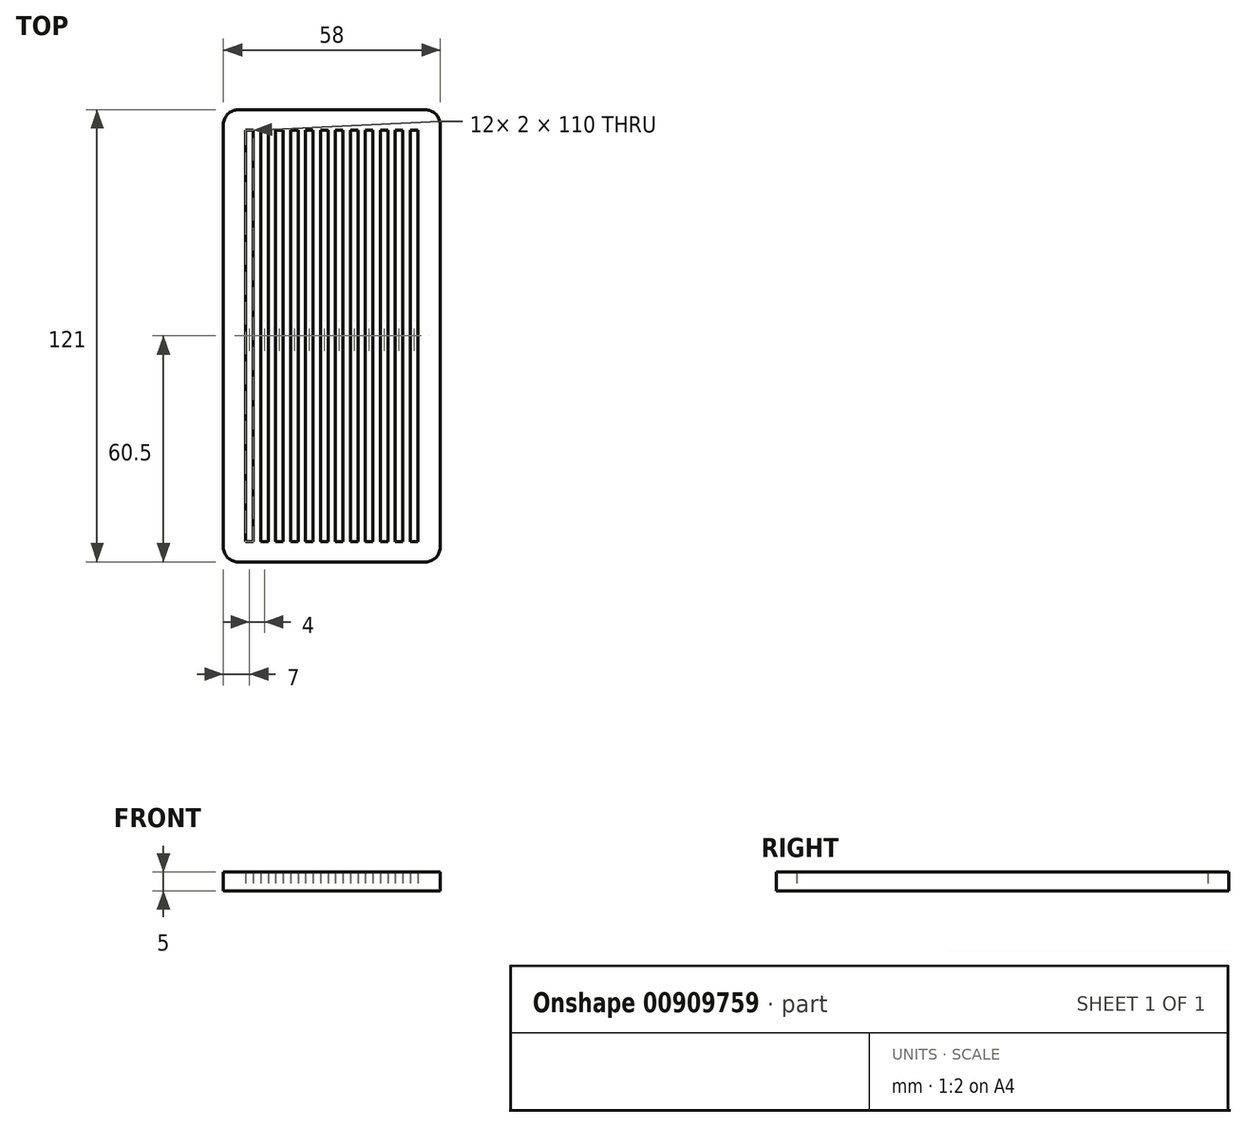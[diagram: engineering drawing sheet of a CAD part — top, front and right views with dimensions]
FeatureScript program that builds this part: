
annotation { "Feature Type Name" : "Feature", "Feature Type Description" : "" }
export const myFeature = defineFeature(function(context is Context, id is Id, definition is map)
    precondition{}
    {
        {
            var Q0;
            Q0=qCreatedBy(makeId("Top.planeOp"),FACE);
            var sketch = newSketch(context, id + "F0", { "sketchPlane" : qUnion([Q0])});
            skLineSegment(sketch, "E0.bottom", {"start": v(29, 60.5) * mm, "end": v(-29, 60.5) * mm});
            skLineSegment(sketch, "E0.top", {"start": v(29, -60.5) * mm, "end": v(-29, -60.5) * mm});
            skLineSegment(sketch, "E0.left", {"start": v(29, 60.5) * mm, "end": v(29, -60.5) * mm});
            skLineSegment(sketch, "E0.right", {"start": v(-29, 60.5) * mm, "end": v(-29, -60.5) * mm});
            skPoint(sketch, "E0.middle", {"position": v(0, 0) * mm});
            skLineSegment(sketch, "E1.bottom", {"start": v(-21, 55) * mm, "end": v(-23, 55) * mm});
            skLineSegment(sketch, "E1.top", {"start": v(-21, -55) * mm, "end": v(-23, -55) * mm});
            skLineSegment(sketch, "E1.left", {"start": v(-21, 55) * mm, "end": v(-21, -55) * mm});
            skLineSegment(sketch, "E1.right", {"start": v(-23, 55) * mm, "end": v(-23, -55) * mm});
            skPoint(sketch, "E1.middle", {"position": v(-22, 0) * mm});
            skLineSegment(sketch, "E2.1.0.0", {"start": v(-17, 55) * mm, "end": v(-17, -55) * mm});
            skLineSegment(sketch, "E2.1.0.1", {"start": v(-19, 55) * mm, "end": v(-19, -55) * mm});
            skLineSegment(sketch, "E2.1.0.2", {"start": v(-17, 55) * mm, "end": v(-19, 55) * mm});
            skLineSegment(sketch, "E2.1.0.3", {"start": v(-17, -55) * mm, "end": v(-19, -55) * mm});
            skLineSegment(sketch, "E2.2.0.0", {"start": v(-13, 55) * mm, "end": v(-13, -55) * mm});
            skLineSegment(sketch, "E2.2.0.1", {"start": v(-15, 55) * mm, "end": v(-15, -55) * mm});
            skLineSegment(sketch, "E2.2.0.2", {"start": v(-13, 55) * mm, "end": v(-15, 55) * mm});
            skLineSegment(sketch, "E2.2.0.3", {"start": v(-13, -55) * mm, "end": v(-15, -55) * mm});
            skLineSegment(sketch, "E2.3.0.0", {"start": v(-9, 55) * mm, "end": v(-9, -55) * mm});
            skLineSegment(sketch, "E2.3.0.1", {"start": v(-11, 55) * mm, "end": v(-11, -55) * mm});
            skLineSegment(sketch, "E2.3.0.2", {"start": v(-9, 55) * mm, "end": v(-11, 55) * mm});
            skLineSegment(sketch, "E2.3.0.3", {"start": v(-9, -55) * mm, "end": v(-11, -55) * mm});
            skLineSegment(sketch, "E2.4.0.0", {"start": v(-5, 55) * mm, "end": v(-5, -55) * mm});
            skLineSegment(sketch, "E2.4.0.1", {"start": v(-7, 55) * mm, "end": v(-7, -55) * mm});
            skLineSegment(sketch, "E2.4.0.2", {"start": v(-5, 55) * mm, "end": v(-7, 55) * mm});
            skLineSegment(sketch, "E2.4.0.3", {"start": v(-5, -55) * mm, "end": v(-7, -55) * mm});
            skLineSegment(sketch, "E2.5.0.0", {"start": v(-1, 55) * mm, "end": v(-1, -55) * mm});
            skLineSegment(sketch, "E2.5.0.1", {"start": v(-3, 55) * mm, "end": v(-3, -55) * mm});
            skLineSegment(sketch, "E2.5.0.2", {"start": v(-1, 55) * mm, "end": v(-3, 55) * mm});
            skLineSegment(sketch, "E2.5.0.3", {"start": v(-1, -55) * mm, "end": v(-3, -55) * mm});
            skLineSegment(sketch, "E2.6.0.0", {"start": v(3, 55) * mm, "end": v(3, -55) * mm});
            skLineSegment(sketch, "E2.6.0.1", {"start": v(1, 55) * mm, "end": v(1, -55) * mm});
            skLineSegment(sketch, "E2.6.0.2", {"start": v(3, 55) * mm, "end": v(1, 55) * mm});
            skLineSegment(sketch, "E2.6.0.3", {"start": v(3, -55) * mm, "end": v(1, -55) * mm});
            skLineSegment(sketch, "E2.7.0.0", {"start": v(7, 55) * mm, "end": v(7, -55) * mm});
            skLineSegment(sketch, "E2.7.0.1", {"start": v(5, 55) * mm, "end": v(5, -55) * mm});
            skLineSegment(sketch, "E2.7.0.2", {"start": v(7, 55) * mm, "end": v(5, 55) * mm});
            skLineSegment(sketch, "E2.7.0.3", {"start": v(7, -55) * mm, "end": v(5, -55) * mm});
            skLineSegment(sketch, "E2.8.0.0", {"start": v(11, 55) * mm, "end": v(11, -55) * mm});
            skLineSegment(sketch, "E2.8.0.1", {"start": v(9, 55) * mm, "end": v(9, -55) * mm});
            skLineSegment(sketch, "E2.8.0.2", {"start": v(11, 55) * mm, "end": v(9, 55) * mm});
            skLineSegment(sketch, "E2.8.0.3", {"start": v(11, -55) * mm, "end": v(9, -55) * mm});
            skLineSegment(sketch, "E2.9.0.0", {"start": v(15, 55) * mm, "end": v(15, -55) * mm});
            skLineSegment(sketch, "E2.9.0.1", {"start": v(13, 55) * mm, "end": v(13, -55) * mm});
            skLineSegment(sketch, "E2.9.0.2", {"start": v(15, 55) * mm, "end": v(13, 55) * mm});
            skLineSegment(sketch, "E2.9.0.3", {"start": v(15, -55) * mm, "end": v(13, -55) * mm});
            skLineSegment(sketch, "E2.10.0.0", {"start": v(19, 55) * mm, "end": v(19, -55) * mm});
            skLineSegment(sketch, "E2.10.0.1", {"start": v(17, 55) * mm, "end": v(17, -55) * mm});
            skLineSegment(sketch, "E2.10.0.2", {"start": v(19, 55) * mm, "end": v(17, 55) * mm});
            skLineSegment(sketch, "E2.10.0.3", {"start": v(19, -55) * mm, "end": v(17, -55) * mm});
            skLineSegment(sketch, "E2.11.0.0", {"start": v(23, 55) * mm, "end": v(23, -55) * mm});
            skLineSegment(sketch, "E2.11.0.1", {"start": v(21, 55) * mm, "end": v(21, -55) * mm});
            skLineSegment(sketch, "E2.11.0.2", {"start": v(23, 55) * mm, "end": v(21, 55) * mm});
            skLineSegment(sketch, "E2.11.0.3", {"start": v(23, -55) * mm, "end": v(21, -55) * mm});
            skLineSegment(sketch, "E2.direction1", {"start": v(-23, -55) * mm, "end": v(-19, -55) * mm, "construction": true});
            skSolve(sketch);
        }
        {
            var Q0;
            Q0 = qSketchRegion(id + "F0", true);
            extrude(context, id + "F1", {"entities" : qUnion([Q0]), "depth" : 5 * mm, "offsetDistance" : 25 * mm});
        }
        {
            var Q0;
            Q0=makeQuery(id+"F1.opExtrude","SWEPT_EDGE",EDGE,{"disambiguationData":[OSD([sQuery(id+"F0.wireOp",EDGE,"E0.bottom"),sQuery(id+"F0.wireOp",EDGE,"E0.left")])]});
            var Q1;
            Q1=makeQuery(id+"F1.opExtrude","SWEPT_EDGE",EDGE,{"disambiguationData":[OSD([sQuery(id+"F0.wireOp",EDGE,"E0.top"),sQuery(id+"F0.wireOp",EDGE,"E0.left")])]});
            var Q2;
            Q2=makeQuery(id+"F1.opExtrude","SWEPT_EDGE",EDGE,{"disambiguationData":[OSD([sQuery(id+"F0.wireOp",EDGE,"E0.top"),sQuery(id+"F0.wireOp",EDGE,"E0.right")])]});
            var Q3;
            Q3=makeQuery(id+"F1.opExtrude","SWEPT_EDGE",EDGE,{"disambiguationData":[OSD([sQuery(id+"F0.wireOp",EDGE,"E0.bottom"),sQuery(id+"F0.wireOp",EDGE,"E0.right")])]});
            fillet(context, id + "F2", {"entities" : qUnion([Q0, Q1, Q2, Q3]), "radius" : 4 * mm, "tangentPropagation" : true, "allowEdgeOverflow" : false});
        }
    });
